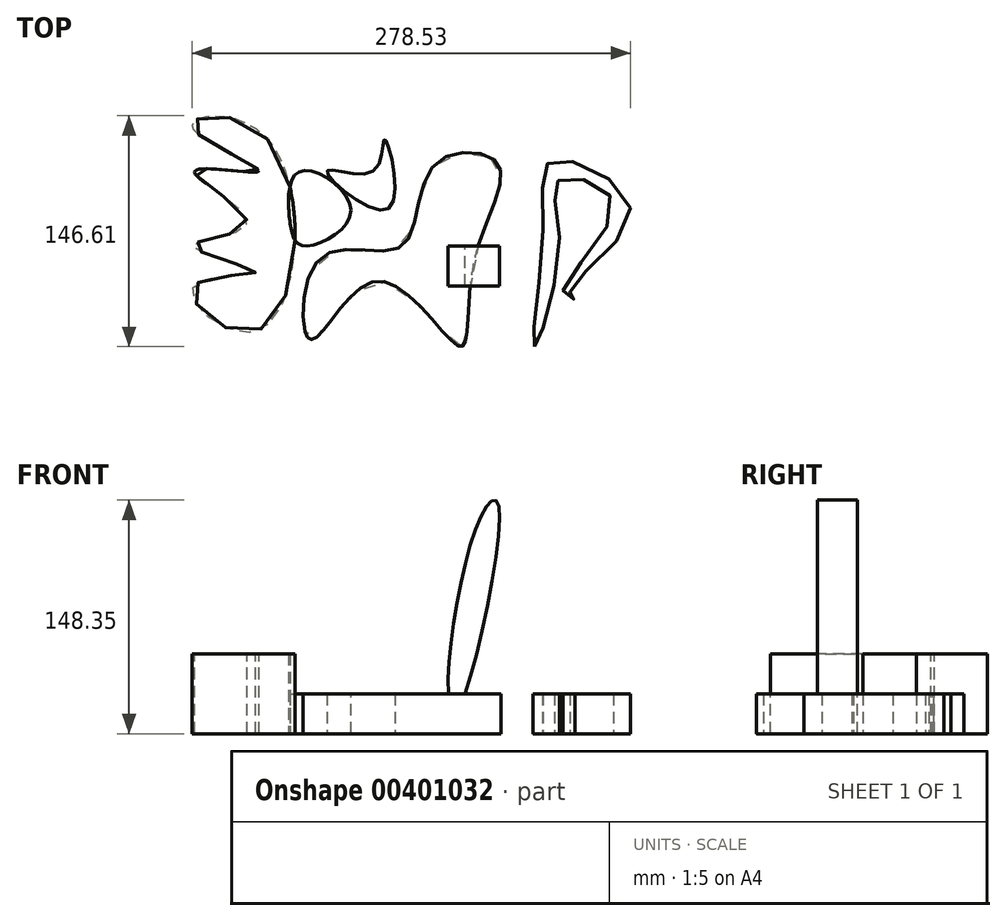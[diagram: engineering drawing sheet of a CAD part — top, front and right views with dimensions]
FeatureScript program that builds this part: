
annotation { "Feature Type Name" : "Feature", "Feature Type Description" : "" }
export const myFeature = defineFeature(function(context is Context, id is Id, definition is map)
    precondition{}
    {
        {
            var Q0;
            Q0=qCreatedBy(makeId("Top.planeOp"),FACE);
            var sketch = newSketch(context, id + "F0", { "sketchPlane" : qUnion([Q0])});
            skFitSpline(sketch, "E0", {"points": [v(-61.66, -54.18) * mm, v(-49.3, -5.74) * mm, v(0, 0) * mm, v(20.75, 51.7) * mm, v(60.64, 52.55) * mm, v(45.46, -10.9) * mm, v(36.72, -63.88) * mm, v(-13.99, -22.35) * mm, v(-55.22, -58.7) * mm, v(-61.66, -54.18) * mm]});
            skFitSpline(sketch, "E1", {"points": [v(-18.39, 47.5) * mm, v(-47.66, 47.36) * mm, v(-8.83, 23.67) * mm, v(-10.82, 67.79) * mm, v(-18.39, 47.5) * mm]});
            skFitSpline(sketch, "E2", {"points": [v(-71.06, 14.57) * mm, v(-64.34, 47.5) * mm, v(-32.5, 22.57) * mm, v(-61.66, 0) * mm, v(-71.06, 14.57) * mm]});
            skFitSpline(sketch, "E3", {"points": [v(-132.62, 0) * mm, v(-98.51, 14.57) * mm, v(-131.7, 47.5) * mm, v(-90.93, 47.5) * mm, v(-132.93, 75.26) * mm, v(-87.74, 70.33) * mm, v(-92.57, -54.18) * mm, v(-132.39, -25.87) * mm, v(-92.94, -16.51) * mm, v(-132.62, 0) * mm]});
            skFitSpline(sketch, "E4", {"points": [v(84, -63.88) * mm, v(89.67, 14.57) * mm, v(97.3, 54.76) * mm, v(145.18, 21.2) * mm, v(106.55, -28.77) * mm, v(109.76, -33.62) * mm, v(102.4, -30.32) * mm, v(134.13, 26.56) * mm, v(100.64, 42.44) * mm, v(99.95, 5.15) * mm, v(84, -63.88) * mm]});
            skSolve(sketch);
        }
        {
            var Q0;
            {var subQ0=sQuery(id+"F0.wireOp",EDGE,"E3");var subQ1=sQuery(id+"F0.wireOp",EDGE,"E2");var subQ2=makeQuery(id+"F0.imprint","INTERSECT",VERTEX,{"disambiguationData":[OD(0.0)],"derivedFrom":[subQ1,subQ0]});Q0=makeQuery(id+"F0.imprint","IMPRINT",FACE,{"disambiguationData":[TD([[makeQuery(id+"F0.imprint","IMPRINT",EDGE,{"disambiguationData":[TD([[subQ2,-1.0]])],"derivedFrom":subQ1}),1.0]])]});}
            var Q1;
            {var subQ0=sQuery(id+"F0.wireOp",EDGE,"E3");var subQ1=sQuery(id+"F0.wireOp",EDGE,"E2");var subQ2=makeQuery(id+"F0.imprint","INTERSECT",VERTEX,{"disambiguationData":[OD(0.0)],"derivedFrom":[subQ1,subQ0]});Q1=makeQuery(id+"F0.imprint","IMPRINT",FACE,{"disambiguationData":[TD([[makeQuery(id+"F0.imprint","IMPRINT",EDGE,{"disambiguationData":[TD([[subQ2,1.0]])],"derivedFrom":subQ1}),-1.0]])]});}
            var Q2;
            Q2=makeQuery(id+"F0.imprint","IMPRINT",FACE,{"disambiguationData":[TD([[makeQuery(id+"F0.imprint","IMPRINT",EDGE,{"derivedFrom":sQuery(id+"F0.wireOp",EDGE,"E1")}),1.0]])]});
            var Q3;
            Q3=makeQuery(id+"F0.imprint","IMPRINT",FACE,{"disambiguationData":[TD([[makeQuery(id+"F0.imprint","IMPRINT",EDGE,{"derivedFrom":sQuery(id+"F0.wireOp",EDGE,"E0")}),-1.0]])]});
            var Q4;
            Q4=makeQuery(id+"F0.imprint","IMPRINT",FACE,{"disambiguationData":[TD([[makeQuery(id+"F0.imprint","IMPRINT",EDGE,{"derivedFrom":sQuery(id+"F0.wireOp",EDGE,"E4")}),-1.0]])]});
            extrude(context, id + "F1", {"entities" : qUnion([Q0, Q1, Q2, Q3, Q4]), "depth" : 25.4 * mm});
        }
        {
            var Q0;
            Q0=qCreatedBy(makeId("Front.planeOp"),FACE);
            var sketch = newSketch(context, id + "F2", { "sketchPlane" : qUnion([Q0])});
            skFitSpline(sketch, "E5", {"points": [v(29.32, 31.9) * mm, v(53.26, 143.8) * mm, v(60.98, 146.2) * mm, v(34.74, 14.3) * mm, v(29.32, 31.9) * mm]});
            skSolve(sketch);
        }
        {
            var Q0;
            Q0=makeQuery(id+"F2.imprint","IMPRINT",FACE,{"disambiguationData":[TD([[makeQuery(id+"F2.imprint","IMPRINT",EDGE,{"derivedFrom":sQuery(id+"F2.wireOp",EDGE,"E5")}),-1.0]])]});
            extrude(context, id + "F3", {"entities" : qUnion([Q0]), "operationType" : NewBodyOperationType.ADD, "depth" : 25.4 * mm});
        }
        {
            var Q0;
            Q0=qCreatedBy(makeId("Top.planeOp"),FACE);
            var sketch = newSketch(context, id + "F4", { "sketchPlane" : qUnion([Q0])});
            skFitSpline(sketch, "E6", {"points": [v(-86.16, 73.83) * mm, v(-75.58, 62.27) * mm, v(-82.99, 54.2) * mm, v(-75.36, 31.46) * mm, v(-86.11, -8.82) * mm, v(-86.04, 20.5) * mm, v(-100.34, 21.7) * mm, v(-95.06, 30.38) * mm, v(-98.43, 50.55) * mm, v(-113.25, 61.96) * mm, v(-100.52, 66.5) * mm, v(-86.16, 73.83) * mm]});
            skSolve(sketch);
        }
        {
            var Q0;
            {var subQ0=sQuery(id+"F0.wireOp",EDGE,"E3");var subQ1=sQuery(id+"F0.wireOp",EDGE,"E2");var subQ2=makeQuery(id+"F0.imprint","INTERSECT",VERTEX,{"disambiguationData":[OD(0.0)],"derivedFrom":[subQ1,subQ0]});Q0=makeQuery(id+"F1.opExtrude","CAP_FACE",FACE,{"disambiguationData":[OSD([subQ1,subQ0]),TDD([makeQuery(id+"F0.imprint","IMPRINT",EDGE,{"disambiguationData":[TD([[subQ2,-1.0]])],"derivedFrom":subQ1}),makeQuery(id+"F0.imprint","IMPRINT",EDGE,{"disambiguationData":[TD([[subQ2,-1.0]])],"derivedFrom":subQ0})])],"isStart":false});}
            extrude(context, id + "F5", {"entities" : qUnion([Q0]), "operationType" : NewBodyOperationType.ADD, "depth" : 25.4 * mm});
        }
        {
            var Q0;
            Q0=sQuery(id+"F4.wireOp",EDGE,"E6");
            extrude(context, id + "F6", {"bodyType" : ToolBodyType.SURFACE, "surfaceEntities" : qUnion([Q0]), "depth" : 76.2 * mm});
        }
    });
